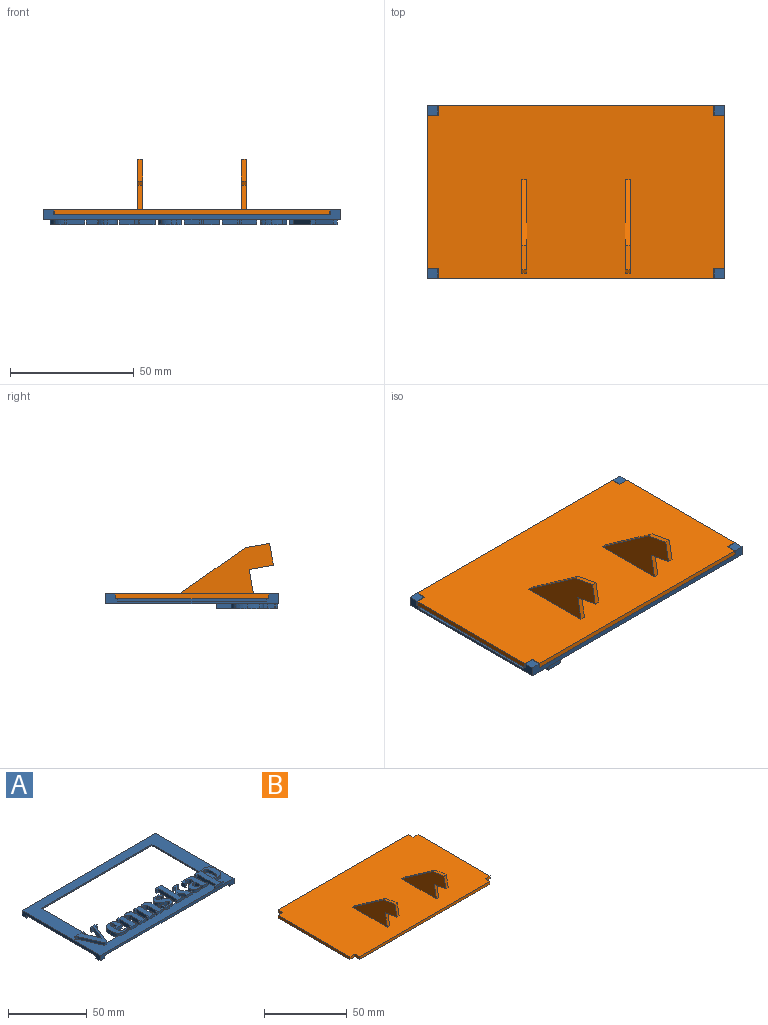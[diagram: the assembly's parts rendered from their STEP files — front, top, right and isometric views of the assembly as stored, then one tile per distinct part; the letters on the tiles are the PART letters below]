
ASSEMBLY  parts=2 mates=1
PART A: 237 faces, bbox 120x70x6 mm
  f0: plane 44.37x1mm, normal (-1,0,0), area 44.4mm2, adj f13,f21,f22,f214
  f1: plane 10.29x3.88mm, normal (0,0,1), area 35.5mm2, adj f14,f215,f216,f232,f233
  f2: plane 1x0.3mm, normal (0,1,0), area 0.3mm2, adj f21,f22,f184,f185
  f3: plane 1.77x1mm, normal (0,1,0), area 1.8mm2, adj f21,f22,f160,f186
  f4: plane 2.08x1mm, normal (0,1,0), area 2.1mm2, adj f21,f22,f157,f158
  f5: plane 2.75x1mm, normal (0,1,0), area 2.8mm2, adj f21,f22,f128,f159
  f6: plane 1.27x1mm, normal (0,1,0), area 1.3mm2, adj f21,f22,f105,f127
  f7: plane 1.59x1mm, normal (0,1,0), area 1.6mm2, adj f21,f22,f102,f103
  f8: plane 1.15x1mm, normal (0,1,0), area 1.1mm2, adj f21,f22,f80,f104
  f9: plane 1.59x1mm, normal (0,1,0), area 1.6mm2, adj f21,f22,f77,f78
  f10: plane 1.73x1mm, normal (0,1,0), area 1.7mm2, adj f21,f22,f55,f79
  f11: plane 11.5x1mm, normal (0,1,0), area 11.5mm2, adj f21,f22,f39,f54
  f12: plane 120x70mm, normal (0,0,-1), area 1646mm2, adj f17,f18,f19,f20,f23,f24,f25,f26
  f13: plane 99x1mm, normal (0,-1,0), area 99mm2, adj f0,f16,f21,f22
  f14: plane 9.95x1mm, normal (-1,0,0), area 10mm2, adj f1,f22,f215,f216
  f15: plane 2.14x1mm, normal (0,1,0), area 2.1mm2, adj f21,f22,f187,f213
  f16: plane 47.74x1mm, normal (1,0,0), area 47.7mm2, adj f13,f21,f22,f38
  f17: plane 70x4mm, normal (1,0,0), area 96mm2, adj f12,f18,f20,f21,f22,f23,f25,f32
  f18: plane 120x4mm, normal (0,1,0), area 256mm2, adj f12,f17,f19,f21,f29,f31,f36,f37
  f19: plane 70x4mm, normal (-1,0,0), area 156mm2, adj f12,f18,f20,f21,f26,f28,f30,f31
  f20: plane 120x4mm, normal (0,-1,0), area 256mm2, adj f12,f17,f19,f21,f27,f28,f33,f34
  f21: plane 120x70mm, normal (0,0,1), area 2616.6mm2, adj f0,f2,f3,f4,f5,f6,f7,f8
  f22: plane 111.5x60mm, normal (0,0,-1), area 1768.6mm2, adj f0,f2,f3,f4,f5,f6,f7,f8
  f23: plane 111.5x1mm, normal (0,1,0), area 111.5mm2, adj f12,f17,f22,f24
  f24: plane 60x1mm, normal (1,0,0), area 60mm2, adj f12,f22,f23,f25
  f25: plane 111.5x1mm, normal (0,-1,0), area 111.5mm2, adj f12,f17,f22,f24
  f26: plane 4x2mm, normal (0,1,0), area 8mm2, adj f12,f19,f27,f28
  f27: plane 4x2mm, normal (1,0,0), area 8mm2, adj f12,f20,f26,f28
  f28: plane 4x4mm, normal (0,0,-1), area 16mm2, adj f19,f20,f26,f27
  f29: plane 4x2mm, normal (1,0,0), area 8mm2, adj f12,f18,f30,f31
  f30: plane 4x2mm, normal (0,-1,0), area 8mm2, adj f12,f19,f29,f31
  f31: plane 4x4mm, normal (0,0,-1), area 16mm2, adj f18,f19,f29,f30
  f32: plane 4x2mm, normal (0,1,0), area 8mm2, adj f12,f17,f33,f34
  f33: plane 4x2mm, normal (-1,0,0), area 8mm2, adj f12,f20,f32,f34
  f34: plane 4x4mm, normal (0,0,-1), area 16mm2, adj f17,f20,f32,f33
  f35: plane 4x2mm, normal (0,-1,0), area 8mm2, adj f12,f17,f36,f37
  f36: plane 4x2mm, normal (-1,0,0), area 8mm2, adj f12,f18,f35,f37
  f37: plane 4x4mm, normal (0,0,-1), area 16mm2, adj f17,f18,f35,f36
  f38: plane 11.77x5.05mm, normal (0.92,0.39,0), area 30.2mm2, adj f16,f21,f22,f40,f41,f53
  f39: plane 17.04x6.94mm, normal (0.93,-0.38,0), area 53.9mm2, adj f11,f21,f22,f46,f47,f53
  f40: plane 2x1.86mm, normal (0.19,-0.98,0), area 3.8mm2, adj f21,f38,f52,f53
  f41: plane 11.77x4.71mm, normal (-0.93,0.37,0), area 38mm2, adj f22,f38,f42,f53
  f42: plane 3x1.81mm, normal (-0.2,-0.98,0), area 5.5mm2, adj f22,f41,f43,f53
  f43: plane 3x0.98mm, normal (-1,0,0), area 2.9mm2, adj f22,f42,f44,f53
  f44: plane 5.29x3mm, normal (0,1,0), area 15.9mm2, adj f22,f43,f45,f53
  f45: plane 3x0.98mm, normal (1,0,0), area 2.9mm2, adj f22,f44,f46,f53
  f46: plane 3x1.7mm, normal (0.21,-0.98,0), area 5.2mm2, adj f22,f39,f45,f53
  f47: plane 2x1.78mm, normal (0,-1,0), area 3.6mm2, adj f21,f39,f48,f53
  f48: plane 17.04x7.3mm, normal (-0.92,-0.39,0), area 37.1mm2, adj f21,f47,f49,f53
  f49: plane 2x1.47mm, normal (-0.24,-0.97,0), area 3mm2, adj f21,f48,f50,f53
  f50: plane 2x0.98mm, normal (-1,0,0), area 2mm2, adj f21,f49,f51,f53
  f51: plane 7.81x2mm, normal (0,1,0), area 15.6mm2, adj f21,f50,f52,f53
  f52: plane 2x0.98mm, normal (1,0,0), area 2mm2, adj f21,f40,f51,f53
  f53: plane 19.19x18.38mm, normal (0,0,1), area 110.4mm2, adj f38,f39,f40,f41,f42,f43,f44,f45
  f54: extruded ~4.57x3mm, area 10.8mm2, adj f11,f21,f22,f61,f74,f76
  f55: plane 3x1.03mm, normal (1,0,0), area 3.1mm2, adj f10,f21,f22,f72,f73,f76
  f56: extruded ~3x0.8mm, area 2.7mm2, adj f22,f57,f75,f76
  f57: extruded ~3x1.2mm, area 4.7mm2, adj f22,f56,f58,f76
  f58: extruded ~3.08x3mm, area 9.4mm2, adj f22,f57,f59,f76
  f59: plane 3x2.92mm, normal (0,1,0), area 8.8mm2, adj f22,f58,f60,f76
  f60: extruded ~3x2.52mm, area 7.6mm2, adj f22,f59,f75,f76
  f61: extruded ~5x3mm, area 16mm2, adj f22,f54,f62,f76
  f62: extruded ~4.92x3mm, area 15.7mm2, adj f22,f61,f63,f76
  f63: extruded ~4.27x3mm, area 14.1mm2, adj f22,f62,f64,f76
  f64: extruded ~3.7x3mm, area 12.2mm2, adj f22,f63,f65,f76
  f65: extruded ~4.25x3mm, area 13.5mm2, adj f22,f64,f66,f76
  f66: plane 3x1.1mm, normal (1,0,0), area 3.3mm2, adj f22,f65,f67,f76
  f67: plane 6.61x3mm, normal (0,-1,0), area 19.8mm2, adj f22,f66,f68,f76
  f68: plane 3x0.21mm, normal (1,0,0), area 0.6mm2, adj f22,f67,f69,f76
  f69: extruded ~3x2.84mm, area 8.6mm2, adj f22,f68,f70,f76
  f70: extruded ~3x1.29mm, area 5.1mm2, adj f22,f69,f71,f76
  f71: extruded ~3x1.98mm, area 6.2mm2, adj f22,f70,f72,f76
  f72: extruded ~3x2.97mm, area 9mm2, adj f22,f55,f71,f76
  f73: extruded ~2x1.91mm, area 4.1mm2, adj f21,f55,f74,f76
  f74: extruded ~2.29x2mm, area 4.6mm2, adj f21,f54,f73,f76
  f75: extruded ~3x1.08mm, area 3.5mm2, adj f22,f56,f60,f76
  f76: plane 13.15x10.53mm, normal (0,0,1), area 80.7mm2, adj f54,f55,f56,f57,f58,f59,f60,f61
  f77: plane 3x0.88mm, normal (-1,0,0), area 1.8mm2, adj f9,f21,f22,f81,f100,f101
  f78: plane 3x0.88mm, normal (1,0,0), area 1.8mm2, adj f9,f21,f22,f87,f88,f101
  f79: plane 3x0.88mm, normal (-1,0,0), area 1.8mm2, adj f10,f21,f22,f88,f89,f101
  f80: plane 3x0.88mm, normal (1,0,0), area 1.8mm2, adj f8,f21,f22,f99,f100,f101
  f81: plane 3x1.13mm, normal (-0.27,0.96,0), area 3.5mm2, adj f22,f77,f82,f101
  f82: plane 7.49x3mm, normal (-1,0,0), area 22.5mm2, adj f22,f81,f83,f101
  f83: extruded ~3x1.76mm, area 5.6mm2, adj f22,f82,f84,f101
  f84: extruded ~3x1.36mm, area 4.7mm2, adj f22,f83,f85,f101
  f85: extruded ~3x2.04mm, area 6.3mm2, adj f22,f84,f86,f101
  f86: plane 9.42x3mm, normal (1,0,0), area 28.2mm2, adj f22,f85,f87,f101
  f87: plane 3x1.15mm, normal (0.27,0.96,0), area 3.6mm2, adj f22,f78,f86,f101
  f88: plane 6.25x2mm, normal (0,-1,0), area 12.5mm2, adj f21,f78,f79,f101
  f89: plane 3x1.23mm, normal (-0.25,0.97,0), area 3.8mm2, adj f22,f79,f90,f101
  f90: plane 10.18x3mm, normal (-1,0,0), area 30.5mm2, adj f22,f89,f91,f101
  f91: plane 3x1.23mm, normal (-0.25,-0.97,0), area 3.8mm2, adj f22,f90,f92,f101
  f92: plane 3x0.89mm, normal (-1,0,0), area 2.7mm2, adj f22,f91,f93,f101
  f93: plane 4.89x3mm, normal (0,1,0), area 14.7mm2, adj f22,f92,f94,f101
  f94: plane 3x1.1mm, normal (0.99,0.17,0), area 3.4mm2, adj f22,f93,f95,f101
  f95: plane 3x0.91mm, normal (-0.46,0.89,0), area 3.1mm2, adj f22,f94,f96,f101
  f96: extruded ~3.37x3mm, area 10.6mm2, adj f22,f95,f97,f101
  f97: extruded ~3.71x3.48mm, area 17.5mm2, adj f22,f96,f98,f101
  f98: plane 8.01x3mm, normal (1,0,0), area 24mm2, adj f22,f97,f99,f101
  f99: plane 3x1.26mm, normal (0.25,0.97,0), area 3.9mm2, adj f22,f80,f98,f101
  f100: plane 6.26x2mm, normal (0,-1,0), area 12.5mm2, adj f21,f77,f80,f101
  f101: plane 14.11x12.93mm, normal (0,0,1), area 108.9mm2, adj f77,f78,f79,f80,f81,f82,f83,f84
  f102: plane 3x0.88mm, normal (-1,0,0), area 1.8mm2, adj f7,f21,f22,f106,f125,f126
  f103: plane 3x0.88mm, normal (1,0,0), area 1.8mm2, adj f7,f21,f22,f112,f113,f126
  f104: plane 3x0.88mm, normal (-1,0,0), area 1.8mm2, adj f8,f21,f22,f113,f114,f126
  f105: plane 3x0.88mm, normal (1,0,0), area 1.8mm2, adj f6,f21,f22,f124,f125,f126
  f106: plane 3x1.13mm, normal (-0.27,0.96,0), area 3.5mm2, adj f22,f102,f107,f126
  f107: plane 7.49x3mm, normal (-1,0,0), area 22.5mm2, adj f22,f106,f108,f126
  f108: extruded ~3x1.76mm, area 5.6mm2, adj f22,f107,f109,f126
  f109: extruded ~3x1.36mm, area 4.7mm2, adj f22,f108,f110,f126
  f110: extruded ~3x2.04mm, area 6.3mm2, adj f22,f109,f111,f126
  f111: plane 9.42x3mm, normal (1,0,0), area 28.2mm2, adj f22,f110,f112,f126
  f112: plane 3x1.15mm, normal (0.27,0.96,0), area 3.6mm2, adj f22,f103,f111,f126
  f113: plane 6.25x2mm, normal (0,-1,0), area 12.5mm2, adj f21,f103,f104,f126
  f114: plane 3x1.23mm, normal (-0.25,0.97,0), area 3.8mm2, adj f22,f104,f115,f126
  f115: plane 10.18x3mm, normal (-1,0,0), area 30.5mm2, adj f22,f114,f116,f126
  f116: plane 3x1.23mm, normal (-0.25,-0.97,0), area 3.8mm2, adj f22,f115,f117,f126
  f117: plane 3x0.89mm, normal (-1,0,0), area 2.7mm2, adj f22,f116,f118,f126
  f118: plane 4.89x3mm, normal (0,1,0), area 14.7mm2, adj f22,f117,f119,f126
  f119: plane 3x1.1mm, normal (0.99,0.17,0), area 3.4mm2, adj f22,f118,f120,f126
  f120: plane 3x0.91mm, normal (-0.46,0.89,0), area 3.1mm2, adj f22,f119,f121,f126
  f121: extruded ~3.37x3mm, area 10.6mm2, adj f22,f120,f122,f126
  f122: extruded ~3.71x3.48mm, area 17.5mm2, adj f22,f121,f123,f126
  f123: plane 8.01x3mm, normal (1,0,0), area 24mm2, adj f22,f122,f124,f126
  f124: plane 3x1.26mm, normal (0.25,0.97,0), area 3.9mm2, adj f22,f105,f123,f126
  f125: plane 6.26x2mm, normal (0,-1,0), area 12.5mm2, adj f21,f102,f105,f126
  f126: plane 14.11x12.93mm, normal (0,0,1), area 108.9mm2, adj f102,f103,f104,f105,f106,f107,f108,f109
  f127: plane 3.43x3mm, normal (-1,0,0), area 9.9mm2, adj f6,f21,f22,f129,f130,f156
  f128: extruded ~3.76x3mm, area 8mm2, adj f5,f21,f22,f154,f155,f156
  f129: extruded ~2x1.86mm, area 3.8mm2, adj f21,f127,f155,f156
  f130: plane 3x0.88mm, normal (0,1,0), area 2.6mm2, adj f22,f127,f131,f156
  f131: plane 3x1.77mm, normal (0.96,0.28,0), area 5.5mm2, adj f22,f130,f132,f156
  f132: extruded ~3x1.23mm, area 4.4mm2, adj f22,f131,f133,f156
  f133: extruded ~3x1.55mm, area 4.8mm2, adj f22,f132,f134,f156
  f134: extruded ~3x1.74mm, area 5.5mm2, adj f22,f133,f135,f156
  f135: extruded ~3x1.28mm, area 4.3mm2, adj f22,f134,f136,f156
  f136: extruded ~3x1.18mm, area 4mm2, adj f22,f135,f137,f156
  f137: extruded ~3x2.4mm, area 7.8mm2, adj f22,f136,f138,f156
  f138: extruded ~3x2.75mm, area 9.8mm2, adj f22,f137,f139,f156
  f139: extruded ~3x2.57mm, area 8.2mm2, adj f22,f138,f140,f156
  f140: extruded ~3x2.73mm, area 9.4mm2, adj f22,f139,f141,f156
  f141: extruded ~3.28x3mm, area 10.5mm2, adj f22,f140,f142,f156
  f142: extruded ~3.71x3mm, area 11.2mm2, adj f22,f141,f143,f156
  f143: plane 3.23x3mm, normal (1,0,0), area 9.7mm2, adj f22,f142,f144,f156
  f144: plane 3x0.88mm, normal (0,-1,0), area 2.6mm2, adj f22,f143,f145,f156
  f145: plane 3x1.47mm, normal (-0.96,-0.28,0), area 4.6mm2, adj f22,f144,f146,f156
  f146: extruded ~3x1.09mm, area 3.8mm2, adj f22,f145,f147,f156
  f147: extruded ~3x1.33mm, area 4.1mm2, adj f22,f146,f148,f156
  f148: extruded ~3x1.43mm, area 4.5mm2, adj f22,f147,f149,f156
  f149: extruded ~3x1.08mm, area 3.6mm2, adj f22,f148,f150,f156
  f150: extruded ~3x1.16mm, area 4mm2, adj f22,f149,f151,f156
  f151: extruded ~3x2.37mm, area 7.7mm2, adj f22,f150,f152,f156
  f152: extruded ~3x2.77mm, area 9.7mm2, adj f22,f151,f153,f156
  f153: extruded ~3x2.46mm, area 7.9mm2, adj f22,f152,f154,f156
  f154: extruded ~3.18x3mm, area 10.7mm2, adj f22,f128,f153,f156
  f155: extruded ~2.24x2mm, area 4.5mm2, adj f21,f128,f129,f156
  f156: plane 13.2x9.17mm, normal (0,0,1), area 67.2mm2, adj f127,f128,f129,f130,f131,f132,f133,f134
  f157: plane 3x0.88mm, normal (-1,0,0), area 1.8mm2, adj f4,f21,f22,f161,f182,f183
  f158: plane 3x0.88mm, normal (1,0,0), area 1.8mm2, adj f4,f21,f22,f165,f166,f183
  f159: plane 3x0.88mm, normal (-1,0,0), area 1.8mm2, adj f5,f21,f22,f166,f167,f183
  f160: plane 3x0.88mm, normal (1,0,0), area 1.8mm2, adj f3,f21,f22,f181,f182,f183
  f161: plane 3x0.73mm, normal (-0.4,0.92,0), area 2.4mm2, adj f22,f157,f162,f183
  f162: plane 4.41x3mm, normal (-0.87,-0.5,0), area 15.2mm2, adj f22,f161,f163,f183
  f163: plane 3x1.54mm, normal (0.57,-0.82,0), area 5.6mm2, adj f22,f162,f164,f183
  f164: plane 3.33x3mm, normal (1,0,0), area 10mm2, adj f22,f163,f165,f183
  f165: plane 3x1.24mm, normal (0.25,0.97,0), area 3.9mm2, adj f22,f158,f164,f183
  f166: plane 6.31x2mm, normal (0,-1,0), area 12.6mm2, adj f21,f158,f159,f183
  f167: plane 3x1.19mm, normal (-0.26,0.97,0), area 3.7mm2, adj f22,f159,f168,f183
  f168: plane 16.62x3mm, normal (-1,0,0), area 49.9mm2, adj f22,f167,f169,f183
  f169: plane 3x1.29mm, normal (-0.24,-0.97,0), area 4mm2, adj f22,f168,f170,f183
  f170: plane 3x0.89mm, normal (-1,0,0), area 2.7mm2, adj f22,f169,f171,f183
  f171: plane 5.16x3mm, normal (0,1,0), area 15.5mm2, adj f22,f170,f172,f183
  f172: plane 13x3mm, normal (1,0,0), area 39mm2, adj f22,f171,f173,f183
  f173: plane 5.36x4.91mm, normal (-0.74,0.68,0), area 21.8mm2, adj f22,f172,f174,f183
  f174: plane 3x1.34mm, normal (-0.22,-0.97,0), area 4.1mm2, adj f22,f173,f175,f183
  f175: plane 3x0.89mm, normal (-1,0,0), area 2.7mm2, adj f22,f174,f176,f183
  f176: plane 4.8x3mm, normal (0,1,0), area 14.4mm2, adj f22,f175,f177,f183
  f177: plane 3x0.89mm, normal (1,0,0), area 2.7mm2, adj f22,f176,f178,f183
  f178: plane 3x1.45mm, normal (0.2,-0.98,0), area 4.4mm2, adj f22,f177,f179,f183
  f179: plane 3.16x3mm, normal (0.73,-0.69,0), area 13.1mm2, adj f22,f178,f180,f183
  f180: plane 7.05x4.33mm, normal (0.85,0.52,0), area 24.8mm2, adj f22,f179,f181,f183
  f181: plane 3x1.12mm, normal (0.28,0.96,0), area 3.5mm2, adj f22,f160,f180,f183
  f182: plane 6.05x2mm, normal (0,-1,0), area 12.1mm2, adj f21,f157,f160,f183
  f183: plane 19.03x14.53mm, normal (0,0,1), area 125.2mm2, adj f157,f158,f159,f160,f161,f162,f163,f164
  f184: plane 3x0.96mm, normal (-0.96,-0.29,0), area 2.2mm2, adj f2,f21,f22,f185,f210,f212
  f185: extruded ~3x1.89mm, area 4.6mm2, adj f2,f21,f22,f184,f194,f212
  f186: extruded ~3.9x3.75mm, area 15.3mm2, adj f3,f21,f22,f194,f195,f212
  f187: plane 3x0.88mm, normal (1,0,0), area 1.8mm2, adj f15,f21,f22,f209,f210,f212
  f188: plane 4.5x3mm, normal (-1,0,0), area 13.5mm2, adj f22,f189,f211,f212
  f189: plane 3x1.12mm, normal (0.03,-1,0), area 3.4mm2, adj f22,f188,f190,f212
  f190: extruded ~3x1.8mm, area 6mm2, adj f22,f189,f191,f212
  f191: extruded ~3x2.04mm, area 6.4mm2, adj f22,f190,f192,f212
  f192: extruded ~3x1.67mm, area 5.2mm2, adj f22,f191,f193,f212
  f193: extruded ~3x1.05mm, area 3.7mm2, adj f22,f192,f211,f212
  f194: extruded ~2x1.7mm, area 3.5mm2, adj f21,f185,f186,f212
  f195: extruded ~3x2.27mm, area 7.1mm2, adj f22,f186,f196,f212
  f196: extruded ~3x1.66mm, area 6.4mm2, adj f22,f195,f197,f212
  f197: extruded ~3.42x3mm, area 10.4mm2, adj f22,f196,f198,f212
  f198: plane 3x1.63mm, normal (-0.02,1,0), area 4.9mm2, adj f22,f197,f199,f212
  f199: plane 3x1.83mm, normal (-1,0,0), area 5.5mm2, adj f22,f198,f200,f212
  f200: extruded ~3x2.28mm, area 10.1mm2, adj f22,f199,f201,f212
  f201: extruded ~3x2.52mm, area 7.9mm2, adj f22,f200,f202,f212
  f202: plane 3x1.57mm, normal (0.95,-0.31,0), area 4.9mm2, adj f22,f201,f203,f212
  f203: plane 3x0.89mm, normal (0,-1,0), area 2.7mm2, adj f22,f202,f204,f212
  f204: plane 3.04x3mm, normal (-1,0,0), area 9.1mm2, adj f22,f203,f205,f212
  f205: extruded ~3x2.97mm, area 9mm2, adj f22,f204,f206,f212
  f206: extruded ~3x1.94mm, area 5.8mm2, adj f22,f205,f207,f212
  f207: extruded ~4.73x3.48mm, area 20.1mm2, adj f22,f206,f208,f212
  f208: plane 8.19x3mm, normal (1,0,0), area 24.6mm2, adj f22,f207,f209,f212
  f209: plane 3x1.26mm, normal (0.25,0.97,0), area 3.9mm2, adj f22,f187,f208,f212
  f210: plane 4.63x2mm, normal (0,-1,0), area 9.3mm2, adj f21,f184,f187,f212
  f211: extruded ~3x1.98mm, area 6.1mm2, adj f22,f188,f193,f212
  f212: plane 13.14x12.42mm, normal (0,0,1), area 92.8mm2, adj f184,f185,f186,f187,f188,f189,f190,f191
  f213: plane 16.02x3mm, normal (-1,0,0), area 42.6mm2, adj f15,f21,f22,f217,f235,f236
  f214: extruded ~3.48x3mm, area 8.4mm2, adj f0,f21,f22,f220,f221,f236
  f215: extruded ~3x2.26mm, area 5.3mm2, adj f1,f14,f22,f232,f234,f236
  f216: extruded ~3x2.29mm, area 5.6mm2, adj f1,f14,f22,f233,f234,f236
  f217: plane 3x1.38mm, normal (-0.23,-0.97,0), area 4.3mm2, adj f22,f213,f218,f236
  f218: plane 3x0.89mm, normal (-1,0,0), area 2.7mm2, adj f22,f217,f219,f236
  f219: plane 5.1x3mm, normal (0,1,0), area 15.3mm2, adj f22,f218,f220,f236
  f220: plane 3x0.64mm, normal (1,0.04,0), area 1.9mm2, adj f22,f214,f219,f236
  f221: extruded ~3.9x2mm, area 8.7mm2, adj f21,f214,f222,f236
  f222: extruded ~4.86x2mm, area 10.3mm2, adj f21,f221,f223,f236
  f223: extruded ~5.04x2mm, area 10.7mm2, adj f21,f222,f224,f236
  f224: extruded ~4.27x2mm, area 9.5mm2, adj f21,f223,f225,f236
  f225: extruded ~2.86x2mm, area 5.8mm2, adj f21,f224,f226,f236
  f226: extruded ~2x1.98mm, area 4mm2, adj f21,f225,f227,f236
  f227: plane 2.74x2mm, normal (1,0,0), area 5.5mm2, adj f21,f226,f228,f236
  f228: plane 2x1.85mm, normal (0.17,0.99,0), area 3.8mm2, adj f21,f227,f229,f236
  f229: plane 2x0.89mm, normal (1,0,0), area 1.8mm2, adj f21,f228,f230,f236
  f230: plane 7.09x2mm, normal (0,-1,0), area 14.2mm2, adj f21,f229,f231,f236
  f231: plane 2x0.89mm, normal (-1,0,0), area 1.8mm2, adj f21,f230,f235,f236
  f232: extruded ~5.28x2.36mm, area 12.8mm2, adj f1,f215,f233,f236
  f233: extruded ~5.01x2.33mm, area 12.2mm2, adj f1,f216,f232,f236
  f234: plane 9.5x3mm, normal (1,0,0), area 28.5mm2, adj f22,f215,f216,f236
  f235: plane 2x1.37mm, normal (-0.23,0.97,0), area 2.8mm2, adj f21,f213,f231,f236
  f236: plane 18.77x13.8mm, normal (0,0,1), area 132.5mm2, adj f213,f214,f215,f216,f217,f218,f219,f220
PART B: 28 faces, bbox 120x70x22.4 mm
  f0: plane 37.96x20.39mm, normal (1,0,0), area 367.8mm2, adj f3,f23,f24,f25,f26,f27
  f1: plane 37.96x20.39mm, normal (-1,0,0), area 367.8mm2, adj f3,f18,f19,f20,f21,f22
  f2: plane 37.96x20.39mm, normal (1,0,0), area 367.8mm2, adj f3,f18,f19,f20,f21,f22
  f3: plane 120x70mm, normal (0,0,1), area 8210.1mm2, adj f0,f1,f2,f4,f5,f6,f7,f8
  f4: plane 4.2x2mm, normal (0,1,0), area 8.4mm2, adj f3,f5,f15,f16
  f5: plane 61.6x2mm, normal (-1,0,0), area 123.2mm2, adj f3,f4,f6,f16
  f6: plane 4.2x2mm, normal (0,-1,0), area 8.4mm2, adj f3,f5,f7,f16
  f7: plane 4.2x2mm, normal (-1,0,0), area 8.4mm2, adj f3,f6,f8,f16
  f8: plane 111.6x2mm, normal (0,-1,0), area 223.2mm2, adj f3,f7,f9,f16
  f9: plane 4.2x2mm, normal (1,0,0), area 8.4mm2, adj f3,f8,f10,f16
  f10: plane 4.2x2mm, normal (0,-1,0), area 8.4mm2, adj f3,f9,f11,f16
  f11: plane 61.6x2mm, normal (1,0,0), area 123.2mm2, adj f3,f10,f12,f16
  f12: plane 4.2x2mm, normal (0,1,0), area 8.4mm2, adj f3,f11,f13,f16
  f13: plane 4.2x2mm, normal (1,0,0), area 8.4mm2, adj f3,f12,f14,f16
  f14: plane 111.6x2mm, normal (0,1,0), area 223.2mm2, adj f3,f13,f15,f16
  f15: plane 4.2x2mm, normal (-1,0,0), area 8.4mm2, adj f3,f4,f14,f16
  f16: plane 120x70mm, normal (0,0,-1), area 8329.4mm2, adj f4,f5,f6,f7,f8,f9,f10,f11
  f17: plane 37.96x20.39mm, normal (-1,0,0), area 367.8mm2, adj f3,f23,f24,f25,f26,f27
  f18: plane 9.85x2mm, normal (0,-0.17,-0.98), area 20mm2, adj f1,f2,f19,f22
  f19: plane 8.81x2mm, normal (0,-0.98,0.17), area 17.9mm2, adj f1,f2,f18,f20
  f20: plane 9.85x2mm, normal (0,0.17,0.98), area 20mm2, adj f1,f2,f19,f21
  f21: plane 26.56x18.65mm, normal (0,0.57,0.82), area 64.9mm2, adj f1,f2,f3,f20
  f22: plane 9.85x2mm, normal (0,-0.98,0.17), area 20mm2, adj f1,f2,f3,f18
  f23: plane 9.85x2mm, normal (0,-0.98,0.17), area 20mm2, adj f0,f3,f17,f27
  f24: plane 26.56x18.65mm, normal (0,0.57,0.82), area 64.9mm2, adj f0,f3,f17,f25
  f25: plane 9.85x2mm, normal (0,0.17,0.98), area 20mm2, adj f0,f17,f24,f26
  f26: plane 8.81x2mm, normal (0,-0.98,0.17), area 17.9mm2, adj f0,f17,f25,f27
  f27: plane 9.85x2mm, normal (0,-0.17,-0.98), area 20mm2, adj f0,f17,f23,f26
PLACE A rot(axis=(0,1,0),180deg) t=(65.23,0.29,8.5)mm
PLACE B t=(-30.27,-4.71,8.5)mm
MATE fastened A.f12 <-> B.f16  axis (0,0,1) through (29.73,-4.71,8.5)mm
